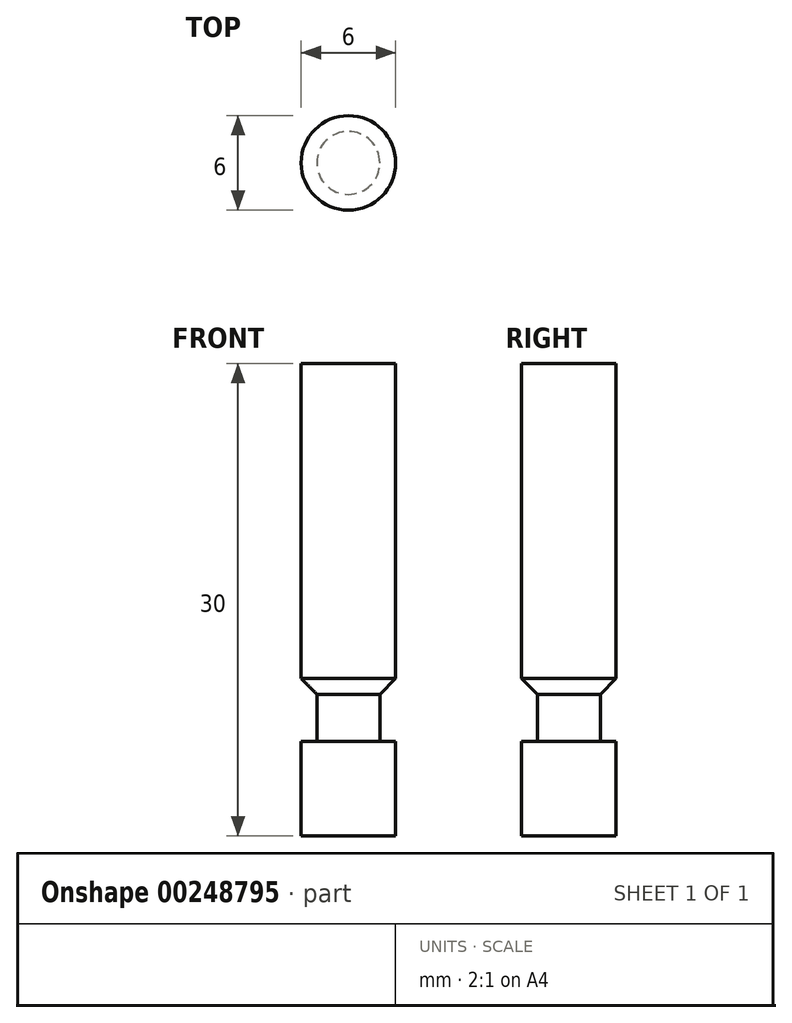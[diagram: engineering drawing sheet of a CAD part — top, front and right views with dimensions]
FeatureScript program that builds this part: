
annotation { "Feature Type Name" : "Feature", "Feature Type Description" : "" }
export const myFeature = defineFeature(function(context is Context, id is Id, definition is map)
    precondition{}
    {
        {
            var Q0;
            Q0=qCreatedBy(makeId("Front.planeOp"),FACE);
            var sketch = newSketch(context, id + "F0", { "sketchPlane" : qUnion([Q0])});
            skLineSegment(sketch, "E0", {"start": v(0, 0) * mm, "end": v(0, 30) * mm});
            skLineSegment(sketch, "E1", {"start": v(0, 30) * mm, "end": v(3, 30) * mm});
            skLineSegment(sketch, "E2", {"start": v(3, 30) * mm, "end": v(3, 10) * mm});
            skLineSegment(sketch, "E3", {"start": v(3, 10) * mm, "end": v(2, 9) * mm});
            skLineSegment(sketch, "E4", {"start": v(2, 9) * mm, "end": v(2, 6) * mm});
            skLineSegment(sketch, "E5", {"start": v(2, 6) * mm, "end": v(3, 6) * mm});
            skLineSegment(sketch, "E6", {"start": v(3, 6) * mm, "end": v(3, 0) * mm});
            skLineSegment(sketch, "E7", {"start": v(3, 0) * mm, "end": v(0, 0) * mm});
            skSolve(sketch);
        }
        {
            var Q0;
            Q0=makeQuery(id+"F0.imprint","IMPRINT",FACE,{"disambiguationData":[TD([[makeQuery(id+"F0.imprint","IMPRINT",EDGE,{"derivedFrom":sQuery(id+"F0.wireOp",EDGE,"E0")}),-1.0]])]});
            var Q1;
            Q1=sQuery(id+"F0.wireOp",EDGE,"E0");
            revolve(context, id + "F1", {"surfaceOperationType" : NewSurfaceOperationType.NEW, "entities" : qUnion([Q0]), "axis" : qUnion([Q1]), "revolveType" : RevolveType.FULL});
        }
    });
